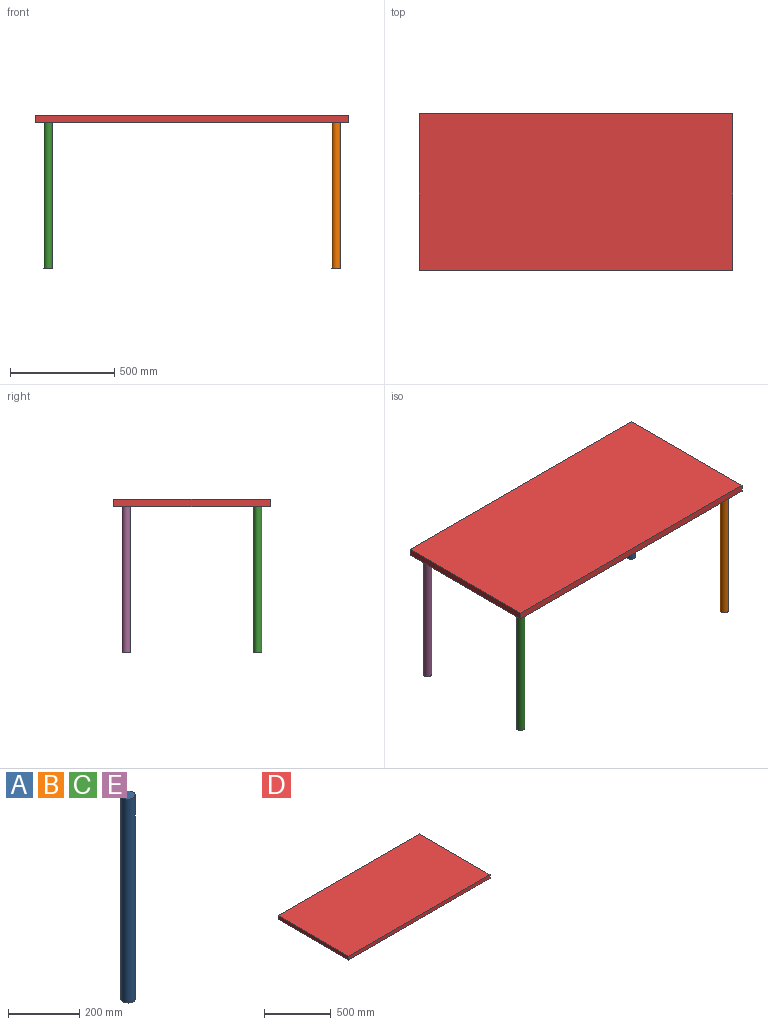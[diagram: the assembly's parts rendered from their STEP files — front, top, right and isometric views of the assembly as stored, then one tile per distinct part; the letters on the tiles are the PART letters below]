
ASSEMBLY  parts=5 mates=4
PART A: 3 faces, bbox 40x40x700 mm
  f0: cylinder r=20mm len=700mm, axis (0,0,1), area 87964.6mm2, adj f1,f2
  f1: plane 40x40mm, normal (0,0,-1), area 1256.6mm2, adj f0
  f2: plane 40x40mm, normal (0,0,1), area 1256.6mm2, adj f0
PART B: same geometry as A
PART C: same geometry as A
PART D: 14 faces, bbox 1500x750x34 mm
  f0: plane 1500x750mm, normal (0,0,-1), area 1124921.5mm2, adj f1,f2,f3,f4,f6,f8,f10,f12
  f1: plane 750x34mm, normal (-1,0,0), area 25500mm2, adj f0,f2,f4,f5
  f2: plane 1500x34mm, normal (0,-1,0), area 51000mm2, adj f0,f1,f3,f5
  f3: plane 750x34mm, normal (1,0,0), area 25500mm2, adj f0,f2,f4,f5
  f4: plane 1500x34mm, normal (0,1,0), area 51000mm2, adj f0,f1,f3,f5
  f5: plane 1500x750mm, normal (0,0,1), area 1125000mm2, adj f1,f2,f3,f4
  f6: cylinder r=2.5mm len=5mm, axis (0,0,-1), area 78.5mm2, adj f0,f7
  f7: plane 5x5mm, normal (0,0,-1), area 19.6mm2, adj f6
  f8: cylinder r=2.5mm len=5mm, axis (0,0,-1), area 78.5mm2, adj f0,f9
  f9: plane 5x5mm, normal (0,0,-1), area 19.6mm2, adj f8
  f10: cylinder r=2.5mm len=5mm, axis (0,0,-1), area 78.5mm2, adj f0,f11
  f11: plane 5x5mm, normal (0,0,-1), area 19.6mm2, adj f10
  f12: cylinder r=2.5mm len=5mm, axis (0,0,-1), area 78.5mm2, adj f0,f13
  f13: plane 5x5mm, normal (0,0,-1), area 19.6mm2, adj f12
PART E: same geometry as A
PLACE A t=(1444.42,767.63,26.01)mm
PLACE B t=(1444.42,137.63,26.01)mm
PLACE C t=(64.42,137.63,26.01)mm
PLACE D t=(4.42,77.63,26.01)mm fixed
PLACE E t=(64.42,767.63,26.01)mm
MATE fastened D.f6 <-> C.f0  axis (0,0,-1) through (64.42,137.63,26.01)mm
MATE fastened B.f0 <-> D.f8  axis (0,0,1) through (1444.42,137.63,26.01)mm
MATE fastened A.f0 <-> D.f10  axis (0,0,1) through (1444.42,767.63,26.01)mm
MATE fastened E.f0 <-> D.f12  axis (0,0,1) through (64.42,767.63,26.01)mm
